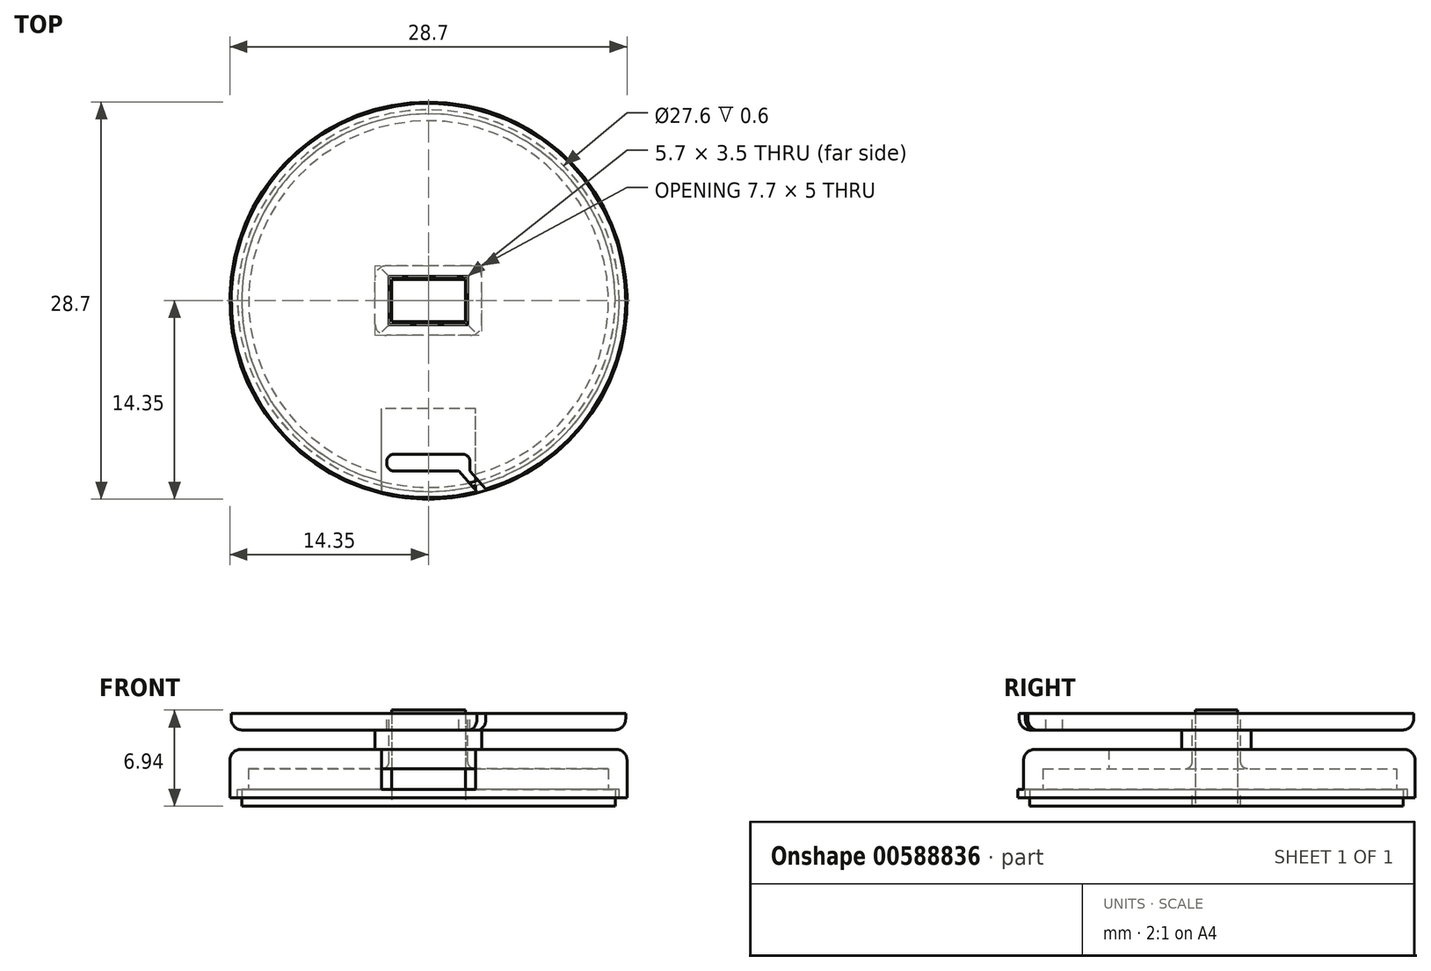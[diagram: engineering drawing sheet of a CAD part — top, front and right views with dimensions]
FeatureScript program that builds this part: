
annotation { "Feature Type Name" : "Feature", "Feature Type Description" : "" }
export const myFeature = defineFeature(function(context is Context, id is Id, definition is map)
    precondition{}
    {
        {
            var Q0;
            Q0=qCreatedBy(makeId("Top.planeOp"),FACE);
            var sketch = newSketch(context, id + "F0", { "sketchPlane" : qUnion([Q0])});
            skCircle(sketch, "E0", {"center": v(0, 0) * mm, "radius": 13.5 * mm});
            skLineSegment(sketch, "E1.bottom", {"start": v(3, -12.42) * mm, "end": v(-3, -12.42) * mm});
            skLineSegment(sketch, "E1.top", {"start": v(3, -8.17) * mm, "end": v(-3, -8.17) * mm});
            skLineSegment(sketch, "E1.left", {"start": v(3, -12.42) * mm, "end": v(3, -8.17) * mm});
            skLineSegment(sketch, "E1.right", {"start": v(-3, -12.42) * mm, "end": v(-3, -8.17) * mm});
            skPoint(sketch, "E1.middle", {"position": v(0, -10.3) * mm});
            skSolve(sketch);
        }
        {
            var Q0;
            Q0=qSketchRegion(id+"F0",true);
            var Q1;
            Q1=makeQuery(id+"F0.imprint","IMPRINT",FACE,{"disambiguationData":[TD([[makeQuery(id+"F0.imprint","IMPRINT",EDGE,{"derivedFrom":sQuery(id+"F0.wireOp",EDGE,"E1.bottom")}),-1.0]])]});
            extrude(context, id + "F1", {"entities" : qUnion([Q0, Q1]), "depth" : 1.2 * mm, "offsetDistance" : 25 * mm});
        }
        {
            var Q0;
            Q0=makeQuery(id+"F0.imprint","IMPRINT",FACE,{"disambiguationData":[TD([[makeQuery(id+"F0.imprint","IMPRINT",EDGE,{"derivedFrom":sQuery(id+"F0.wireOp",EDGE,"E1.bottom")}),-1.0]])]});
            extrude(context, id + "F2", {"entities" : qUnion([Q0]), "operationType" : NewBodyOperationType.ADD, "depth" : 4.2 * mm, "offsetDistance" : 25 * mm});
        }
        {
            var Q0;
            Q0=makeQuery(id+"F1.opExtrude","CAP_FACE",FACE,{"disambiguationData":[OSD([sQuery(id+"F0.wireOp",EDGE,"E0")])],"isStart":false});
            var sketch = newSketch(context, id + "F3", { "sketchPlane" : qUnion([Q0])});
            skCircle(sketch, "E2", {"center": v(0, 0) * mm, "radius": 14.35 * mm});
            skCircle(sketch, "E3", {"center": v(0, 0) * mm, "radius": 13.8 * mm});
            skLineSegment(sketch, "E4.bottom", {"start": v(3.4, -12.8) * mm, "end": v(-3.4, -12.8) * mm});
            skLineSegment(sketch, "E4.top", {"start": v(3.4, -7.8) * mm, "end": v(-3.4, -7.8) * mm});
            skLineSegment(sketch, "E4.left", {"start": v(3.4, -12.8) * mm, "end": v(3.4, -7.8) * mm});
            skLineSegment(sketch, "E4.right", {"start": v(-3.4, -12.8) * mm, "end": v(-3.4, -7.8) * mm});
            skPoint(sketch, "E4.middle", {"position": v(0, -10.3) * mm});
            skCircle(sketch, "E5", {"center": v(0, 0) * mm, "radius": 13 * mm});
            skLineSegment(sketch, "E6.bottom", {"start": v(2.67, -1.52) * mm, "end": v(-2.67, -1.53) * mm});
            skLineSegment(sketch, "E6.top", {"start": v(2.67, 1.53) * mm, "end": v(-2.67, 1.52) * mm});
            skLineSegment(sketch, "E6.left", {"start": v(2.67, -1.52) * mm, "end": v(2.67, 1.53) * mm});
            skLineSegment(sketch, "E6.right", {"start": v(-2.67, -1.53) * mm, "end": v(-2.67, 1.52) * mm});
            skSolve(sketch);
        }
        {
            var Q0;
            {var subQ0=sQuery(id+"F3.wireOp",EDGE,"E4.top");Q0=makeQuery(id+"F3.imprint","IMPRINT",FACE,{"disambiguationData":[TD([[makeQuery(id+"F3.imprint","IMPRINT",EDGE,{"derivedFrom":subQ0}),-1.0]])]});}
            var Q1;
            Q1=makeQuery(id+"F3.imprint","IMPRINT",FACE,{"disambiguationData":[TD([[makeQuery(id+"F3.imprint","IMPRINT",EDGE,{"derivedFrom":makeQuery(id+"F1.opExtrude","CAP_EDGE",EDGE,{"disambiguationData":[OSD([sQuery(id+"F0.wireOp",EDGE,"E0")])],"isStart":false})}),1.0]])]});
            var Q2;
            {var subQ0=sQuery(id+"F3.wireOp",EDGE,"E5");var subQ1=sQuery(id+"F3.wireOp",EDGE,"E4.bottom");var subQ2=makeQuery(id+"F3.imprint","INTERSECT",VERTEX,{"disambiguationData":[OD(0.0)],"derivedFrom":[subQ1,subQ0]});Q2=makeQuery(id+"F3.imprint","IMPRINT",FACE,{"disambiguationData":[TD([[makeQuery(id+"F3.imprint","IMPRINT",EDGE,{"disambiguationData":[TD([[subQ2,-1.0]])],"derivedFrom":subQ1}),1.0]])]});}
            var Q3;
            Q3=makeQuery(id+"F3.imprint","IMPRINT",FACE,{"disambiguationData":[TD([[makeQuery(id+"F3.imprint","IMPRINT",EDGE,{"derivedFrom":sQuery(id+"F3.wireOp",EDGE,"E3")}),1.0]])]});
            var Q4;
            Q4=makeQuery(id+"F3.imprint","IMPRINT",FACE,{"disambiguationData":[TD([[makeQuery(id+"F3.imprint","IMPRINT",EDGE,{"derivedFrom":sQuery(id+"F3.wireOp",EDGE,"E2")}),1.0]])]});
            extrude(context, id + "F4", {"entities" : qUnion([Q0, Q1, Q2, Q3, Q4]), "depth" : 2.9 * mm, "offsetDistance" : 25 * mm});
        }
        {
            var Q0;
            Q0=makeQuery(id+"F3.imprint","IMPRINT",FACE,{"disambiguationData":[TD([[makeQuery(id+"F3.imprint","IMPRINT",EDGE,{"derivedFrom":sQuery(id+"F3.wireOp",EDGE,"E2")}),1.0]])]});
            extrude(context, id + "F5", {"entities" : qUnion([Q0]), "operationType" : NewBodyOperationType.ADD, "oppositeDirection" : true, "depth" : 0.6 * mm, "offsetDistance" : 25 * mm});
        }
        {
            var Q0;
            {var subQ0=sQuery(id+"F3.wireOp",EDGE,"E4.top");Q0=makeQuery(id+"F3.imprint","IMPRINT",FACE,{"disambiguationData":[TD([[makeQuery(id+"F3.imprint","IMPRINT",EDGE,{"derivedFrom":subQ0}),-1.0]])]});}
            var Q1;
            {var subQ1=sQuery(id+"F3.wireOp",EDGE,"E4.top");Q1=makeQuery(id+"F3.imprint","IMPRINT",FACE,{"disambiguationData":[TD([[makeQuery(id+"F3.imprint","IMPRINT",EDGE,{"derivedFrom":subQ1}),1.0]])]});}
            var Q2;
            {var subQ0=sQuery(id+"F3.wireOp",EDGE,"E5");var subQ1=sQuery(id+"F3.wireOp",EDGE,"E4.bottom");var subQ2=makeQuery(id+"F3.imprint","INTERSECT",VERTEX,{"disambiguationData":[OD(0.0)],"derivedFrom":[subQ1,subQ0]});Q2=makeQuery(id+"F3.imprint","IMPRINT",FACE,{"disambiguationData":[TD([[makeQuery(id+"F3.imprint","IMPRINT",EDGE,{"disambiguationData":[TD([[subQ2,-1.0]])],"derivedFrom":subQ1}),1.0]])]});}
            var Q3;
            {var subQ0=makeQuery(id+"F1.opExtrude","CAP_FACE",FACE,{"disambiguationData":[OSD([sQuery(id+"F0.wireOp",EDGE,"E0")])],"isStart":false});Q3=makeQuery(id+"F3.imprint","IMPRINT",FACE,{"disambiguationData":[TD([[makeQuery(id+"F3.imprint","IMPRINT",EDGE,{"derivedFrom":makeQuery(id+"F2.boolean.opBoolean","INTERSECT",EDGE,{"derivedFrom":[subQ0,makeQuery(id+"F2.opExtrude","SWEPT_FACE",FACE,{"disambiguationData":[OSD([sQuery(id+"F0.wireOp",EDGE,"E1.bottom")])]})]})}),1.0]])]});}
            var Q4;
            Q4=sQuery(id+"F3.wireOp",EDGE,"E5");
            extrude(context, id + "F6", {"entities" : qUnion([Q0, Q1, Q2, Q3]), "operationType" : NewBodyOperationType.REMOVE, "surfaceEntities" : qUnion([Q4]), "depth" : 1.5 * mm, "offsetDistance" : 25 * mm});
        }
        {
            var Q0;
            Q0=makeQuery(id+"F2.opExtrude","SWEPT_FACE",FACE,{"disambiguationData":[OSD([sQuery(id+"F0.wireOp",EDGE,"E1.bottom")])]});
            var sketch = newSketch(context, id + "F7", { "sketchPlane" : qUnion([Q0])});
            skLineSegment(sketch, "E7.bottom", {"start": v(-3.4, 4.2) * mm, "end": v(3.4, 4.2) * mm});
            skLineSegment(sketch, "E7.top", {"start": v(-3.4, 1.2) * mm, "end": v(3.4, 1.2) * mm});
            skLineSegment(sketch, "E7.left", {"start": v(-3.4, 4.2) * mm, "end": v(-3.4, 1.2) * mm});
            skLineSegment(sketch, "E7.right", {"start": v(3.4, 4.2) * mm, "end": v(3.4, 1.2) * mm});
            skSolve(sketch);
        }
        {
            var Q0;
            Q0=qSketchRegion(id+"F7",true);
            extrude(context, id + "F8", {"entities" : qUnion([Q0]), "operationType" : NewBodyOperationType.REMOVE, "depth" : 8 * mm, "offsetDistance" : 25 * mm});
        }
        {
            var Q0;
            Q0=makeQuery(id+"F3.imprint","IMPRINT",FACE,{"disambiguationData":[TD([[makeQuery(id+"F3.imprint","IMPRINT",EDGE,{"derivedFrom":sQuery(id+"F3.wireOp",EDGE,"E6.bottom")}),-1.0]])]});
            extrude(context, id + "F9", {"entities" : qUnion([Q0]), "operationType" : NewBodyOperationType.ADD, "depth" : 5.75 * mm, "offsetDistance" : 25 * mm});
        }
        {
            var Q0;
            Q0=makeQuery(id+"F4.opExtrude","CAP_FACE",FACE,{"disambiguationData":[OSD([sQuery(id+"F3.wireOp",EDGE,"E2"),sQuery(id+"F3.wireOp",EDGE,"E4.bottom"),sQuery(id+"F3.wireOp",EDGE,"E4.top"),sQuery(id+"F3.wireOp",EDGE,"E4.left"),sQuery(id+"F3.wireOp",EDGE,"E4.right"),sQuery(id+"F3.wireOp",EDGE,"E6.bottom"),sQuery(id+"F3.wireOp",EDGE,"E6.top"),sQuery(id+"F3.wireOp",EDGE,"E6.left"),sQuery(id+"F3.wireOp",EDGE,"E6.right")])],"isStart":false});
            var sketch = newSketch(context, id + "F10", { "sketchPlane" : qUnion([Q0])});
            skLineSegment(sketch, "E8.bottom", {"start": v(3.85, -2.5) * mm, "end": v(-3.85, -2.5) * mm});
            skLineSegment(sketch, "E8.top", {"start": v(3.85, 2.5) * mm, "end": v(-3.85, 2.5) * mm});
            skLineSegment(sketch, "E8.left", {"start": v(3.85, -2.5) * mm, "end": v(3.85, 2.5) * mm});
            skLineSegment(sketch, "E8.right", {"start": v(-3.85, -2.5) * mm, "end": v(-3.85, 2.5) * mm});
            skPoint(sketch, "E8.middle", {"position": v(0, 0) * mm});
            skSolve(sketch);
        }
        {
            var Q0;
            Q0=makeQuery(id+"F10.imprint","IMPRINT",FACE,{"disambiguationData":[TD([[makeQuery(id+"F10.imprint","IMPRINT",EDGE,{"derivedFrom":sQuery(id+"F10.wireOp",EDGE,"E8.bottom")}),-1.0]])]});
            extrude(context, id + "F11", {"entities" : qUnion([Q0]), "operationType" : NewBodyOperationType.ADD, "depth" : 2.6 * mm, "offsetDistance" : 25 * mm});
        }
        {
            var Q0;
            Q0=makeQuery(id+"F11.opExtrude","CAP_FACE",FACE,{"disambiguationData":[OSD([sQuery(id+"F3.wireOp",EDGE,"E6.bottom"),sQuery(id+"F3.wireOp",EDGE,"E6.top"),sQuery(id+"F3.wireOp",EDGE,"E6.left"),sQuery(id+"F3.wireOp",EDGE,"E6.right"),sQuery(id+"F10.wireOp",EDGE,"E8.bottom"),sQuery(id+"F10.wireOp",EDGE,"E8.top"),sQuery(id+"F10.wireOp",EDGE,"E8.left"),sQuery(id+"F10.wireOp",EDGE,"E8.right")])],"isStart":false});
            var sketch = newSketch(context, id + "F12", { "sketchPlane" : qUnion([Q0])});
            skCircle(sketch, "E9", {"center": v(0, 0) * mm, "radius": 14.25 * mm});
            skLineSegment(sketch, "E10.bottom", {"start": v(2.85, -1.75) * mm, "end": v(-2.85, -1.75) * mm});
            skLineSegment(sketch, "E10.top", {"start": v(2.85, 1.75) * mm, "end": v(-2.85, 1.75) * mm});
            skLineSegment(sketch, "E10.left", {"start": v(2.85, -1.75) * mm, "end": v(2.85, 1.75) * mm});
            skLineSegment(sketch, "E10.right", {"start": v(-2.85, -1.75) * mm, "end": v(-2.85, 1.75) * mm});
            skSolve(sketch);
        }
        {
            var Q0;
            Q0=makeQuery(id+"F4.opExtrude","CAP_EDGE",EDGE,{"disambiguationData":[OSD([sQuery(id+"F3.wireOp",EDGE,"E2")])],"isStart":false});
            var Q1;
            Q1=makeQuery(id+"F11.opExtrude","SWEPT_EDGE",EDGE,{"disambiguationData":[OSD([sQuery(id+"F10.wireOp",EDGE,"E8.bottom"),sQuery(id+"F10.wireOp",EDGE,"E8.right")])]});
            var Q2;
            Q2=makeQuery(id+"F11.opExtrude","SWEPT_EDGE",EDGE,{"disambiguationData":[OSD([sQuery(id+"F10.wireOp",EDGE,"E8.bottom"),sQuery(id+"F10.wireOp",EDGE,"E8.left")])]});
            var Q3;
            Q3=makeQuery(id+"F11.opExtrude","SWEPT_EDGE",EDGE,{"disambiguationData":[OSD([sQuery(id+"F10.wireOp",EDGE,"E8.top"),sQuery(id+"F10.wireOp",EDGE,"E8.left")])]});
            var Q4;
            Q4=makeQuery(id+"F11.opExtrude","SWEPT_EDGE",EDGE,{"disambiguationData":[OSD([sQuery(id+"F10.wireOp",EDGE,"E8.top"),sQuery(id+"F10.wireOp",EDGE,"E8.right")])]});
            fillet(context, id + "F13", {"entities" : qUnion([Q0, Q1, Q2, Q3, Q4]), "radius" : 0.8 * mm, "tangentPropagation" : true, "allowEdgeOverflow" : false});
        }
        {
            var Q0;
            Q0=makeQuery(id+"F12.imprint","IMPRINT",FACE,{"disambiguationData":[TD([[makeQuery(id+"F12.imprint","IMPRINT",EDGE,{"derivedFrom":sQuery(id+"F12.wireOp",EDGE,"E10.bottom")}),-1.0]])]});
            extrude(context, id + "F14", {"entities" : qUnion([Q0]), "operationType" : NewBodyOperationType.REMOVE, "oppositeDirection" : true, "depth" : 7.8 * mm, "offsetDistance" : 25 * mm});
        }
        {
            var Q0;
            Q0=makeQuery(id+"F12.imprint","IMPRINT",FACE,{"disambiguationData":[TD([[makeQuery(id+"F12.imprint","IMPRINT",EDGE,{"derivedFrom":sQuery(id+"F12.wireOp",EDGE,"E9")}),1.0]])]});
            var Q1;
            Q1=makeQuery(id+"F12.imprint","IMPRINT",FACE,{"disambiguationData":[TD([[makeQuery(id+"F12.imprint","IMPRINT",EDGE,{"derivedFrom":sQuery(id+"F12.wireOp",EDGE,"E10.bottom")}),1.0]])]});
            extrude(context, id + "F15", {"entities" : qUnion([Q0, Q1]), "operationType" : NewBodyOperationType.ADD, "oppositeDirection" : true, "depth" : 1.2 * mm, "offsetDistance" : 25 * mm});
        }
        {
            var Q0;
            Q0=makeQuery(id+"F15.opExtrude","CAP_EDGE",EDGE,{"disambiguationData":[OSD([sQuery(id+"F12.wireOp",EDGE,"E9")])],"isStart":false});
            fillet(context, id + "F16", {"entities" : qUnion([Q0]), "radius" : 0.8 * mm, "tangentPropagation" : true, "allowEdgeOverflow" : false});
        }
        {
            var Q0;
            Q0=makeQuery(id+"F15.boolean.opBoolean","MERGE",FACE,{"derivedFrom":[makeQuery(id+"F11.opExtrude","CAP_FACE",FACE,{"disambiguationData":[OSD([sQuery(id+"F3.wireOp",EDGE,"E6.bottom"),sQuery(id+"F3.wireOp",EDGE,"E6.top"),sQuery(id+"F3.wireOp",EDGE,"E6.left"),sQuery(id+"F3.wireOp",EDGE,"E6.right"),sQuery(id+"F10.wireOp",EDGE,"E8.bottom"),sQuery(id+"F10.wireOp",EDGE,"E8.top"),sQuery(id+"F10.wireOp",EDGE,"E8.left"),sQuery(id+"F10.wireOp",EDGE,"E8.right")])],"isStart":false}),makeQuery(id+"F15.opExtrude","CAP_FACE",FACE,{"disambiguationData":[OSD([sQuery(id+"F12.wireOp",EDGE,"E9"),sQuery(id+"F12.wireOp",EDGE,"E10.bottom"),sQuery(id+"F12.wireOp",EDGE,"E10.top"),sQuery(id+"F12.wireOp",EDGE,"E10.left"),sQuery(id+"F12.wireOp",EDGE,"E10.right")])],"isStart":true})]});
            var sketch = newSketch(context, id + "F17", { "sketchPlane" : qUnion([Q0])});
            skLineSegment(sketch, "E11.top", {"start": v(2.5, -11.11) * mm, "end": v(-2.5, -11.11) * mm});
            skLineSegment(sketch, "E11.left", {"start": v(3, -12.31) * mm, "end": v(3, -11.61) * mm});
            skLineSegment(sketch, "E11.right", {"start": v(-3, -11.81) * mm, "end": v(-3, -11.61) * mm});
            skPoint(sketch, "E11.middle", {"position": v(0, -11.71) * mm});
            skLineSegment(sketch, "E12.trimOffspring", {"start": v(2.2, -12.31) * mm, "end": v(-2.5, -12.31) * mm});
            skPoint(sketch, "E13.visualSharp", {"position": v(-3, -11.11) * mm});
            skArc(sketch, "E13.filletArc", {"start": v(-2.5, -11.11) * mm, "mid": v(-2.85, -11.26) * mm, "end": v(-3, -11.61) * mm});
            skPoint(sketch, "E14.visualSharp", {"position": v(-3, -12.31) * mm});
            skArc(sketch, "E14.filletArc", {"start": v(-3, -11.81) * mm, "mid": v(-2.85, -12.17) * mm, "end": v(-2.5, -12.31) * mm});
            skPoint(sketch, "E15.visualSharp", {"position": v(3, -11.11) * mm});
            skArc(sketch, "E15.filletArc", {"start": v(3, -11.61) * mm, "mid": v(2.85, -11.26) * mm, "end": v(2.5, -11.11) * mm});
            skLineSegment(sketch, "E16", {"start": v(2.2, -12.31) * mm, "end": v(3.69, -14.02) * mm});
            skLineSegment(sketch, "E17", {"start": v(3.69, -14.02) * mm, "end": v(4.49, -14.02) * mm});
            skLineSegment(sketch, "E18", {"start": v(4.49, -14.02) * mm, "end": v(3, -12.31) * mm});
            skSolve(sketch);
        }
        {
            var Q0;
            Q0 = qSketchRegion(id + "F17", true);
            extrude(context, id + "F18", {"entities" : qUnion([Q0]), "operationType" : NewBodyOperationType.REMOVE, "oppositeDirection" : true, "depth" : 1.5 * mm, "offsetDistance" : 25 * mm});
        }
        {
            var Q0;
            Q0=makeQuery(id+"F14.boolean.opBoolean","COPY",EDGE,{"derivedFrom":makeQuery(id+"F14.opExtrude","CAP_EDGE",EDGE,{"disambiguationData":[OSD([sQuery(id+"F12.wireOp",EDGE,"E10.bottom")])],"isStart":true})});
            var Q1;
            Q1=makeQuery(id+"F14.boolean.opBoolean","COPY",EDGE,{"derivedFrom":makeQuery(id+"F14.opExtrude","CAP_EDGE",EDGE,{"disambiguationData":[OSD([sQuery(id+"F12.wireOp",EDGE,"E10.left")])],"isStart":true})});
            var Q2;
            Q2=makeQuery(id+"F14.boolean.opBoolean","COPY",EDGE,{"derivedFrom":makeQuery(id+"F14.opExtrude","CAP_EDGE",EDGE,{"disambiguationData":[OSD([sQuery(id+"F12.wireOp",EDGE,"E10.top")])],"isStart":true})});
            var Q3;
            Q3=makeQuery(id+"F14.boolean.opBoolean","COPY",EDGE,{"derivedFrom":makeQuery(id+"F14.opExtrude","CAP_EDGE",EDGE,{"disambiguationData":[OSD([sQuery(id+"F12.wireOp",EDGE,"E10.right")])],"isStart":true})});
            var Q4;
            {var subQ0=sQuery(id+"F3.wireOp",EDGE,"E6.bottom");var subQ1=sQuery(id+"F3.wireOp",EDGE,"E6.top");var subQ2=sQuery(id+"F3.wireOp",EDGE,"E6.left");var subQ3=sQuery(id+"F3.wireOp",EDGE,"E6.right");var subQ4=sQuery(id+"F3.wireOp",EDGE,"E5");Q4=makeQuery(id+"F14.boolean.opBoolean","INTERSECT",EDGE,{"derivedFrom":[makeQuery(id+"F6.boolean.opBoolean","COPY",FACE,{"disambiguationData":[TD([makeQuery(id+"F4.opExtrude","SWEPT_FACE",FACE,{"disambiguationData":[OSD([sQuery(id+"F3.wireOp",EDGE,"E4.top")])]})])],"derivedFrom":makeQuery(id+"F6.opExtrude","CAP_FACE",FACE,{"disambiguationData":[OSD([subQ4,subQ0,subQ1,subQ2,subQ3])],"isStart":false})}),makeQuery(id+"F14.opExtrude","SWEPT_FACE",FACE,{"disambiguationData":[OSD([sQuery(id+"F12.wireOp",EDGE,"E10.bottom")])]})]});}
            var Q5;
            {var subQ0=sQuery(id+"F3.wireOp",EDGE,"E6.bottom");var subQ1=sQuery(id+"F3.wireOp",EDGE,"E6.top");var subQ2=sQuery(id+"F3.wireOp",EDGE,"E6.left");var subQ3=sQuery(id+"F3.wireOp",EDGE,"E6.right");var subQ4=sQuery(id+"F3.wireOp",EDGE,"E5");Q5=makeQuery(id+"F14.boolean.opBoolean","INTERSECT",EDGE,{"derivedFrom":[makeQuery(id+"F6.boolean.opBoolean","COPY",FACE,{"disambiguationData":[TD([makeQuery(id+"F4.opExtrude","SWEPT_FACE",FACE,{"disambiguationData":[OSD([sQuery(id+"F3.wireOp",EDGE,"E4.top")])]})])],"derivedFrom":makeQuery(id+"F6.opExtrude","CAP_FACE",FACE,{"disambiguationData":[OSD([subQ4,subQ0,subQ1,subQ2,subQ3])],"isStart":false})}),makeQuery(id+"F14.opExtrude","SWEPT_FACE",FACE,{"disambiguationData":[OSD([sQuery(id+"F12.wireOp",EDGE,"E10.left")])]})]});}
            var Q6;
            {var subQ0=sQuery(id+"F3.wireOp",EDGE,"E6.bottom");var subQ1=sQuery(id+"F3.wireOp",EDGE,"E6.top");var subQ2=sQuery(id+"F3.wireOp",EDGE,"E6.left");var subQ3=sQuery(id+"F3.wireOp",EDGE,"E6.right");var subQ4=sQuery(id+"F3.wireOp",EDGE,"E5");Q6=makeQuery(id+"F14.boolean.opBoolean","INTERSECT",EDGE,{"derivedFrom":[makeQuery(id+"F6.boolean.opBoolean","COPY",FACE,{"disambiguationData":[TD([makeQuery(id+"F4.opExtrude","SWEPT_FACE",FACE,{"disambiguationData":[OSD([sQuery(id+"F3.wireOp",EDGE,"E4.top")])]})])],"derivedFrom":makeQuery(id+"F6.opExtrude","CAP_FACE",FACE,{"disambiguationData":[OSD([subQ4,subQ0,subQ1,subQ2,subQ3])],"isStart":false})}),makeQuery(id+"F14.opExtrude","SWEPT_FACE",FACE,{"disambiguationData":[OSD([sQuery(id+"F12.wireOp",EDGE,"E10.top")])]})]});}
            var Q7;
            {var subQ0=sQuery(id+"F3.wireOp",EDGE,"E6.bottom");var subQ1=sQuery(id+"F3.wireOp",EDGE,"E6.top");var subQ2=sQuery(id+"F3.wireOp",EDGE,"E6.left");var subQ3=sQuery(id+"F3.wireOp",EDGE,"E6.right");var subQ4=sQuery(id+"F3.wireOp",EDGE,"E5");Q7=makeQuery(id+"F14.boolean.opBoolean","INTERSECT",EDGE,{"derivedFrom":[makeQuery(id+"F6.boolean.opBoolean","COPY",FACE,{"disambiguationData":[TD([makeQuery(id+"F4.opExtrude","SWEPT_FACE",FACE,{"disambiguationData":[OSD([sQuery(id+"F3.wireOp",EDGE,"E4.top")])]})])],"derivedFrom":makeQuery(id+"F6.opExtrude","CAP_FACE",FACE,{"disambiguationData":[OSD([subQ4,subQ0,subQ1,subQ2,subQ3])],"isStart":false})}),makeQuery(id+"F14.opExtrude","SWEPT_FACE",FACE,{"disambiguationData":[OSD([sQuery(id+"F12.wireOp",EDGE,"E10.right")])]})]});}
            fillet(context, id + "F19", {"entities" : qUnion([Q0, Q1, Q2, Q3, Q4, Q5, Q6, Q7]), "radius" : 0.5 * mm, "tangentPropagation" : true, "allowEdgeOverflow" : false});
        }
        {
            var Q0;
            Q0=makeQuery(id+"F1.opExtrude","SWEPT_BODY",BODY,{"disambiguationData":[OSD([sQuery(id+"F0.wireOp",EDGE,"E0")])]});
            deleteBodies(context, id + "F20", {"entities" : qUnion([Q0])});
        }
    });
